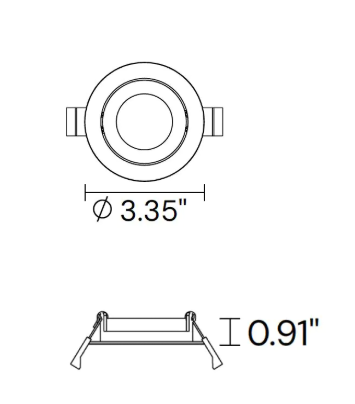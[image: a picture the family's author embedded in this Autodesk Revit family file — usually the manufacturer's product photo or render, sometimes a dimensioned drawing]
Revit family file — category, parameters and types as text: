
# Revit family: Alcon-14078-6 -Revit-Family
name_source: partatom
category: Lighting Fixtures
units: mm (PartAtom-declared; Revit-internal decimal feet)

## family parameters
Always vertical = Yes
Cut with Voids When Loaded = No
Host = Ceiling
Light Source = Yes
OmniClass Number = 23.80.70.11
OmniClass Title = Luminaries for Internal Lighting
Part Type = Normal
Room Calculation Point = No
Round Connector Dimension = Use Diameter
Shared = No

## types (1)
- Type 1
    Color Filter = 16777215
    Default Elevation = 0' - 0"
    Dimming Lamp Color Temperature Shift = <None>
    Housing = Default
    Light Source Symbol Length = 10' - 0"
    LightSource = light
    Link To Product Page = https://www.alconlighting.com
    Manufacturer = Alcon Light
    Product Identity = Alcon Lighting 14078-6
    Reflector = Default metal
    Spot Beam Angle = 30.00°
    Spot Field Angle = 90.00°
    Tilt Angle = 60.00°

## geometry (parser evidence)
native form markers: Sweep x2
no freeform markers — native parametric forms only
